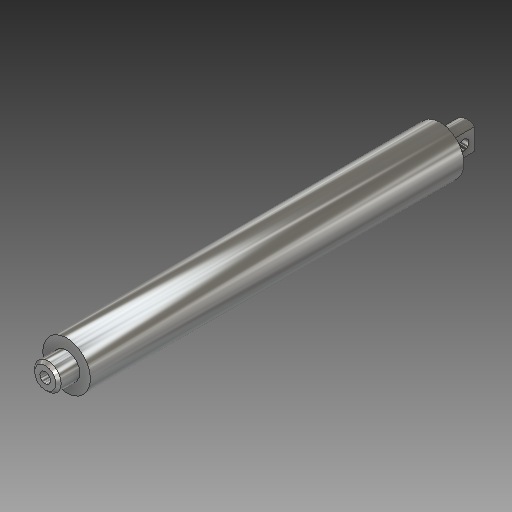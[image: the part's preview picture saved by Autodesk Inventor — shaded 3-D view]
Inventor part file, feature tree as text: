
AUTODESK INVENTOR PART (.ipt)
format: ipt  version: 2017 SP1 (Build 210196100, 196)  size: 156,160 bytes
history: native  units: in
note: dims shown in document units (in); Inventor stores cm internally (conversion verified against a paired STEP export)
features: extrude x5, sketch x5, chamfer x1
ambient origin geometry x8: Origin, YZ Plane, XZ Plane, XY Plane, X Axis, Y Axis, Z Axis, Center Point
bodies: Solid1 (feature_tree)
feature tree (11):
  extrude  "Extrusion1"  Depth=8.75in TaperAngle=0.0deg
  extrude  "Extrusion2"  Depth=0.3125in
  extrude  "Extrusion3"  Depth=0.625in
  extrude  "Extrusion4"  Depth=0.625in TaperAngle=0.0deg
  chamfer  "Chamfer1"  Distance=0.5in
  extrude  "Extrusion5"  Depth=0.125in TaperAngle=45.0deg
  sketch  "Sketch1"  dims[d0=1.118in d1=8.75in d2=0.0in]
  sketch  "Sketch2"  dims[d3=0.375in d4=0.3125in]
  sketch  "Sketch3"  dims[d5=0.625in d6=0.0in d7=0.26in]
  sketch  "Sketch4"  dims[d8=0.25in d9=0.625in d10=0.0in]
  sketch  "Sketch5"  dims[d11=0.625in d12=0.5in d13=0.0in d14=0.0625in d15=0.125in d16=45.0deg d17=0.25in d18=6.0in d19=0.0in]
